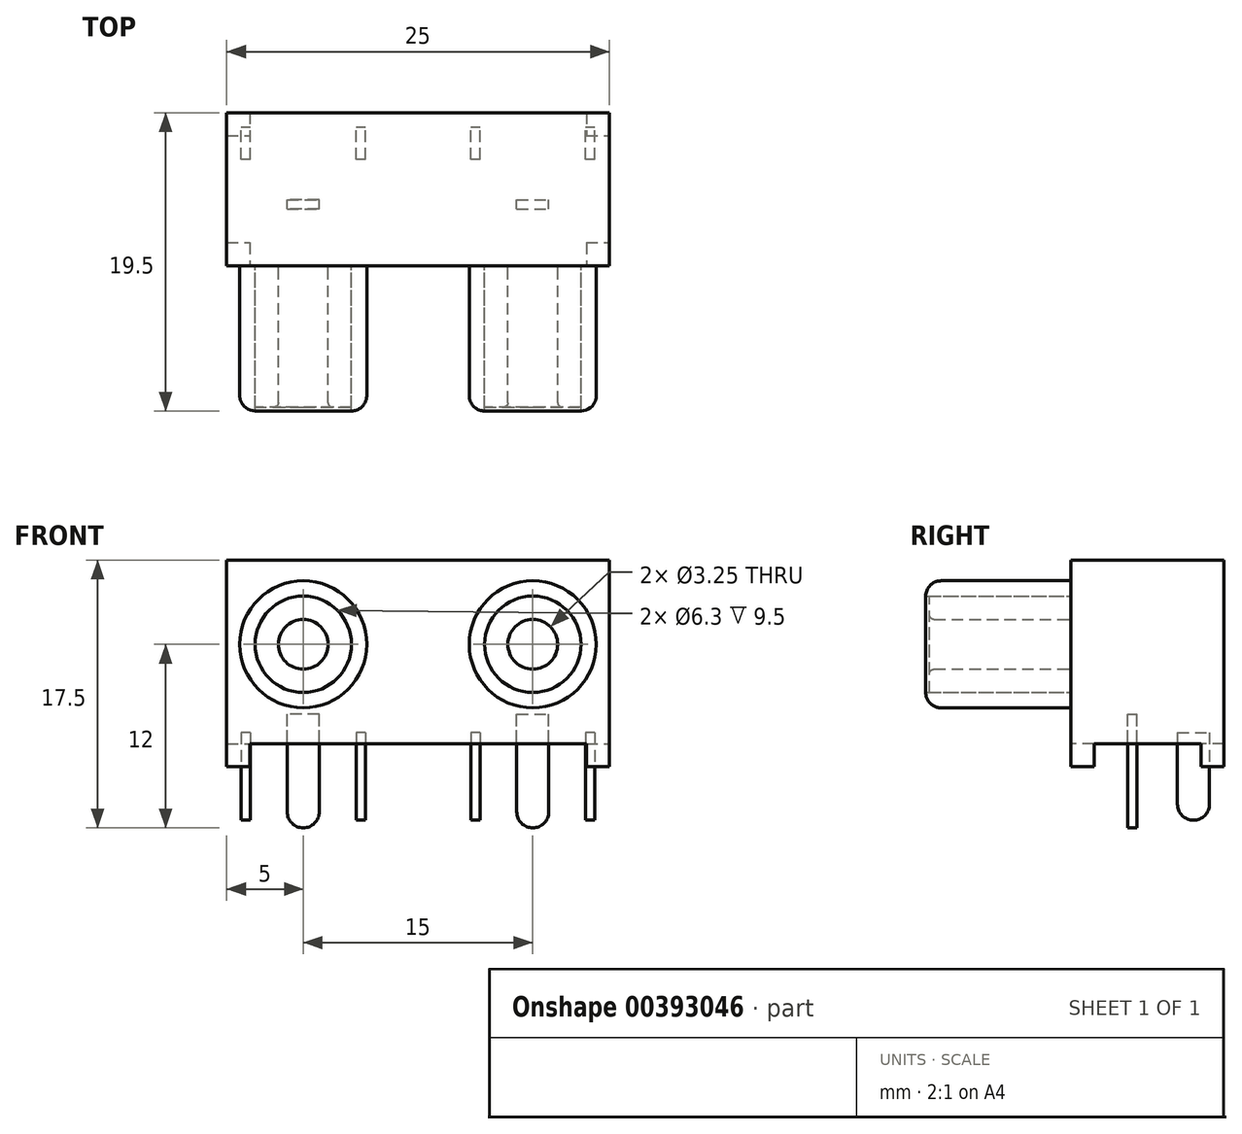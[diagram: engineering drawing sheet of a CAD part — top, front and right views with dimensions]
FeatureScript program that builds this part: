
annotation { "Feature Type Name" : "Feature", "Feature Type Description" : "" }
export const myFeature = defineFeature(function(context is Context, id is Id, definition is map)
    precondition{}
    {
        {
            var Q0;
            Q0=qCreatedBy(makeId("Front.planeOp"),FACE);
            var sketch = newSketch(context, id + "F0", { "sketchPlane" : qUnion([Q0])});
            skCircle(sketch, "E0", {"center": v(-7.5, 0) * mm, "radius": 4.15 * mm});
            skCircle(sketch, "E1", {"center": v(7.5, 0) * mm, "radius": 4.15 * mm});
            skLineSegment(sketch, "E2", {"start": v(-12.5, 5.5) * mm, "end": v(12.5, 5.5) * mm});
            skLineSegment(sketch, "E3", {"start": v(12.5, 5.5) * mm, "end": v(12.5, -8) * mm});
            skLineSegment(sketch, "E4", {"start": v(12.5, -8) * mm, "end": v(11, -8) * mm});
            skLineSegment(sketch, "E5", {"start": v(11, -8) * mm, "end": v(11, -6.5) * mm});
            skLineSegment(sketch, "E6", {"start": v(11, -6.5) * mm, "end": v(-11, -6.5) * mm});
            skLineSegment(sketch, "E7", {"start": v(-11, -6.5) * mm, "end": v(-11, -8) * mm});
            skLineSegment(sketch, "E8", {"start": v(-12.5, 5.5) * mm, "end": v(-12.5, -8) * mm});
            skLineSegment(sketch, "E9", {"start": v(-12.5, -8) * mm, "end": v(-11, -8) * mm});
            skCircle(sketch, "E10", {"center": v(-7.5, 0) * mm, "radius": 1.63 * mm});
            skCircle(sketch, "E11", {"center": v(7.5, 0) * mm, "radius": 1.63 * mm});
            skCircle(sketch, "E12", {"center": v(-7.5, 0) * mm, "radius": 3.15 * mm});
            skCircle(sketch, "E13", {"center": v(7.5, 0) * mm, "radius": 3.15 * mm});
            skSolve(sketch);
        }
        {
            var Q0;
            Q0=makeQuery(id+"F0.imprint","IMPRINT",FACE,{"disambiguationData":[TD([[makeQuery(id+"F0.imprint","IMPRINT",EDGE,{"derivedFrom":sQuery(id+"F0.wireOp",EDGE,"E0")}),1.0]])]});
            var Q1;
            Q1=makeQuery(id+"F0.imprint","IMPRINT",FACE,{"disambiguationData":[TD([[makeQuery(id+"F0.imprint","IMPRINT",EDGE,{"derivedFrom":sQuery(id+"F0.wireOp",EDGE,"E1")}),1.0]])]});
            extrude(context, id + "F1", {"entities" : qUnion([Q0, Q1]), "depth" : 9.5 * mm});
        }
        {
            var Q0;
            Q0=makeQuery(id+"F0.imprint","IMPRINT",FACE,{"disambiguationData":[TD([[makeQuery(id+"F0.imprint","IMPRINT",EDGE,{"derivedFrom":sQuery(id+"F0.wireOp",EDGE,"E10")}),-1.0]])]});
            var Q1;
            Q1=makeQuery(id+"F0.imprint","IMPRINT",FACE,{"disambiguationData":[TD([[makeQuery(id+"F0.imprint","IMPRINT",EDGE,{"derivedFrom":sQuery(id+"F0.wireOp",EDGE,"E11")}),-1.0]])]});
            extrude(context, id + "F2", {"entities" : qUnion([Q0, Q1]), "depth" : 9.25 * mm});
        }
        {
            var Q0;
            Q0=makeQuery(id+"F1.opExtrude","CAP_EDGE",EDGE,{"disambiguationData":[OSD([sQuery(id+"F0.wireOp",EDGE,"E0")])],"isStart":false});
            var Q1;
            Q1=makeQuery(id+"F1.opExtrude","CAP_EDGE",EDGE,{"disambiguationData":[OSD([sQuery(id+"F0.wireOp",EDGE,"E1")])],"isStart":false});
            fillet(context, id + "F3", {"entities" : qUnion([Q0, Q1]), "radius" : 1 * mm, "tangentPropagation" : true, "allowEdgeOverflow" : false});
        }
        {
            var Q0;
            Q0=makeQuery(id+"F0.imprint","IMPRINT",FACE,{"disambiguationData":[TD([[makeQuery(id+"F0.imprint","IMPRINT",EDGE,{"derivedFrom":sQuery(id+"F0.wireOp",EDGE,"E0")}),-1.0]])]});
            var Q1;
            Q1=makeQuery(id+"F0.imprint","IMPRINT",FACE,{"disambiguationData":[TD([[makeQuery(id+"F0.imprint","IMPRINT",EDGE,{"derivedFrom":sQuery(id+"F0.wireOp",EDGE,"E1")}),1.0]])]});
            var Q2;
            Q2=makeQuery(id+"F0.imprint","IMPRINT",FACE,{"disambiguationData":[TD([[makeQuery(id+"F0.imprint","IMPRINT",EDGE,{"derivedFrom":sQuery(id+"F0.wireOp",EDGE,"E11")}),-1.0]])]});
            var Q3;
            Q3=makeQuery(id+"F0.imprint","IMPRINT",FACE,{"disambiguationData":[TD([[makeQuery(id+"F0.imprint","IMPRINT",EDGE,{"derivedFrom":sQuery(id+"F0.wireOp",EDGE,"E11")}),1.0]])]});
            var Q4;
            Q4=makeQuery(id+"F0.imprint","IMPRINT",FACE,{"disambiguationData":[TD([[makeQuery(id+"F0.imprint","IMPRINT",EDGE,{"derivedFrom":sQuery(id+"F0.wireOp",EDGE,"E10")}),-1.0]])]});
            var Q5;
            Q5=makeQuery(id+"F0.imprint","IMPRINT",FACE,{"disambiguationData":[TD([[makeQuery(id+"F0.imprint","IMPRINT",EDGE,{"derivedFrom":sQuery(id+"F0.wireOp",EDGE,"E0")}),1.0]])]});
            var Q6;
            Q6=makeQuery(id+"F0.imprint","IMPRINT",FACE,{"disambiguationData":[TD([[makeQuery(id+"F0.imprint","IMPRINT",EDGE,{"derivedFrom":sQuery(id+"F0.wireOp",EDGE,"E10")}),1.0]])]});
            extrude(context, id + "F4", {"entities" : qUnion([Q0, Q1, Q2, Q3, Q4, Q5, Q6]), "oppositeDirection" : true, "depth" : 10 * mm});
        }
        {
            var Q0;
            Q0=makeQuery(id+"F4.opExtrude","SWEPT_FACE",FACE,{"disambiguationData":[OSD([sQuery(id+"F0.wireOp",EDGE,"E3")])]});
            cPlane(context, id + "F5", {"entities" : qUnion([Q0]), "cplaneType" : CPlaneType.OFFSET, "offset" : 0 * mm, "width" : 150 * mm, "height" : 150 * mm});
        }
        {
            var Q0;
            Q0=qCreatedBy(id+"F5.planeOp",FACE);
            var sketch = newSketch(context, id + "F6", { "sketchPlane" : qUnion([Q0])});
            skLineSegment(sketch, "E14", {"start": v(1.5, -8) * mm, "end": v(1.5, -6.5) * mm});
            skLineSegment(sketch, "E15", {"start": v(1.5, -6.5) * mm, "end": v(8.5, -6.5) * mm});
            skLineSegment(sketch, "E16", {"start": v(8.5, -6.5) * mm, "end": v(8.5, -8) * mm});
            skLineSegment(sketch, "E17", {"start": v(1.5, -8) * mm, "end": v(8.5, -8) * mm});
            skSolve(sketch);
        }
        {
            var Q0;
            Q0=makeQuery(id+"F6.imprint","IMPRINT",FACE,{"disambiguationData":[TD([[makeQuery(id+"F6.imprint","IMPRINT",EDGE,{"derivedFrom":sQuery(id+"F6.wireOp",EDGE,"E14")}),-1.0]])]});
            extrude(context, id + "F7", {"entities" : qUnion([Q0]), "operationType" : NewBodyOperationType.REMOVE, "oppositeDirection" : true, "depth" : 25 * mm});
        }
        {
            var Q0;
            Q0=qCreatedBy(makeId("Front.planeOp"),FACE);
            cPlane(context, id + "F8", {"entities" : qUnion([Q0]), "cplaneType" : CPlaneType.OFFSET, "offset" : 4 * mm, "oppositeDirection" : true, "width" : 150 * mm, "height" : 150 * mm});
        }
        {
            var Q0;
            Q0=qCreatedBy(id+"F8.planeOp",FACE);
            var sketch = newSketch(context, id + "F9", { "sketchPlane" : qUnion([Q0])});
            skLineSegment(sketch, "E18.top", {"start": v(-6.45, -4.58) * mm, "end": v(-8.55, -4.58) * mm});
            skLineSegment(sketch, "E18.left", {"start": v(-6.45, -10.95) * mm, "end": v(-6.45, -4.58) * mm});
            skLineSegment(sketch, "E18.right", {"start": v(-8.55, -10.95) * mm, "end": v(-8.55, -4.58) * mm});
            skArc(sketch, "E19", {"start": v(-8.55, -10.95) * mm, "mid": v(-7.5, -12) * mm, "end": v(-6.45, -10.95) * mm});
            skLineSegment(sketch, "E20.MirrorCS", {"start": v(8.55, -10.95) * mm, "end": v(8.55, -4.58) * mm});
            skLineSegment(sketch, "E21.MirrorCS", {"start": v(6.45, -10.95) * mm, "end": v(6.45, -4.58) * mm});
            skLineSegment(sketch, "E22.MirrorCS", {"start": v(6.45, -4.58) * mm, "end": v(8.55, -4.58) * mm});
            skArc(sketch, "E23.MirrorCS", {"start": v(8.55, -10.95) * mm, "mid": v(7.5, -12) * mm, "end": v(6.45, -10.95) * mm});
            skSolve(sketch);
        }
        {
            var Q0;
            Q0=makeQuery(id+"F9.imprint","IMPRINT",FACE,{"disambiguationData":[TD([[makeQuery(id+"F9.imprint","IMPRINT",EDGE,{"derivedFrom":sQuery(id+"F9.wireOp",EDGE,"E18.top")}),1.0]])]});
            var Q1;
            Q1=makeQuery(id+"F9.imprint","IMPRINT",FACE,{"disambiguationData":[TD([[makeQuery(id+"F9.imprint","IMPRINT",EDGE,{"derivedFrom":sQuery(id+"F9.wireOp",EDGE,"E20.MirrorCS")}),1.0]])]});
            extrude(context, id + "F10", {"entities" : qUnion([Q0, Q1]), "depth" : 0.3 * mm, "hasSecondDirection" : true, "secondDirectionOppositeDirection" : true, "secondDirectionDepth" : 0.3 * mm});
        }
        {
            var Q0;
            Q0=qCreatedBy(makeId("Right.planeOp"),FACE);
            cPlane(context, id + "F11", {"entities" : qUnion([Q0]), "cplaneType" : CPlaneType.OFFSET, "offset" : 3.75 * mm, "width" : 150 * mm, "height" : 150 * mm});
        }
        {
            var Q0;
            Q0=qCreatedBy(makeId("Right.planeOp"),FACE);
            cPlane(context, id + "F12", {"entities" : qUnion([Q0]), "cplaneType" : CPlaneType.OFFSET, "offset" : 11.25 * mm, "width" : 150 * mm, "height" : 150 * mm});
        }
        {
            var Q0;
            Q0=qCreatedBy(makeId("Right.planeOp"),FACE);
            cPlane(context, id + "F13", {"entities" : qUnion([Q0]), "cplaneType" : CPlaneType.OFFSET, "offset" : 3.75 * mm, "oppositeDirection" : true, "width" : 150 * mm, "height" : 150 * mm});
        }
        {
            var Q0;
            Q0=qCreatedBy(makeId("Right.planeOp"),FACE);
            cPlane(context, id + "F14", {"entities" : qUnion([Q0]), "cplaneType" : CPlaneType.OFFSET, "offset" : 11.25 * mm, "oppositeDirection" : true, "width" : 150 * mm, "height" : 150 * mm});
        }
        {
            var Q0;
            Q0=qCreatedBy(id+"F12.planeOp",FACE);
            var sketch = newSketch(context, id + "F15", { "sketchPlane" : qUnion([Q0])});
            skLineSegment(sketch, "E24.bottom", {"start": v(6.95, -5.78) * mm, "end": v(9.05, -5.78) * mm});
            skLineSegment(sketch, "E24.left", {"start": v(6.95, -5.78) * mm, "end": v(6.95, -10.45) * mm});
            skLineSegment(sketch, "E24.right", {"start": v(9.05, -5.78) * mm, "end": v(9.05, -10.45) * mm});
            skArc(sketch, "E25", {"start": v(6.95, -10.45) * mm, "mid": v(8, -11.5) * mm, "end": v(9.05, -10.45) * mm});
            skSolve(sketch);
        }
        {
            var Q0;
            Q0=qCreatedBy(id+"F11.planeOp",FACE);
            var sketch = newSketch(context, id + "F16", { "sketchPlane" : qUnion([Q0])});
            skLineSegment(sketch, "E26.bottom", {"start": v(6.95, -5.78) * mm, "end": v(9.05, -5.78) * mm});
            skLineSegment(sketch, "E26.left", {"start": v(6.95, -5.78) * mm, "end": v(6.95, -10.45) * mm});
            skLineSegment(sketch, "E26.right", {"start": v(9.05, -5.78) * mm, "end": v(9.05, -10.45) * mm});
            skArc(sketch, "E27", {"start": v(6.95, -10.45) * mm, "mid": v(8, -11.5) * mm, "end": v(9.05, -10.45) * mm});
            skSolve(sketch);
        }
        {
            var Q0;
            Q0=qCreatedBy(id+"F13.planeOp",FACE);
            var sketch = newSketch(context, id + "F17", { "sketchPlane" : qUnion([Q0])});
            skLineSegment(sketch, "E28.bottom", {"start": v(6.95, -5.78) * mm, "end": v(9.05, -5.78) * mm});
            skLineSegment(sketch, "E28.left", {"start": v(6.95, -5.78) * mm, "end": v(6.95, -10.45) * mm});
            skLineSegment(sketch, "E28.right", {"start": v(9.05, -5.78) * mm, "end": v(9.05, -10.45) * mm});
            skArc(sketch, "E29", {"start": v(6.95, -10.45) * mm, "mid": v(8, -11.5) * mm, "end": v(9.05, -10.45) * mm});
            skSolve(sketch);
        }
        {
            var Q0;
            Q0=qCreatedBy(id+"F14.planeOp",FACE);
            var sketch = newSketch(context, id + "F18", { "sketchPlane" : qUnion([Q0])});
            skLineSegment(sketch, "E30.bottom", {"start": v(6.95, -5.78) * mm, "end": v(9.05, -5.78) * mm});
            skLineSegment(sketch, "E30.left", {"start": v(6.95, -5.78) * mm, "end": v(6.95, -10.45) * mm});
            skLineSegment(sketch, "E30.right", {"start": v(9.05, -5.78) * mm, "end": v(9.05, -10.45) * mm});
            skArc(sketch, "E31", {"start": v(6.95, -10.45) * mm, "mid": v(8, -11.5) * mm, "end": v(9.05, -10.45) * mm});
            skSolve(sketch);
        }
        {
            var Q0;
            Q0=makeQuery(id+"F18.imprint","IMPRINT",FACE,{"disambiguationData":[TD([[makeQuery(id+"F18.imprint","IMPRINT",EDGE,{"derivedFrom":sQuery(id+"F18.wireOp",EDGE,"E30.bottom")}),-1.0]])]});
            var Q1;
            Q1=makeQuery(id+"F17.imprint","IMPRINT",FACE,{"disambiguationData":[TD([[makeQuery(id+"F17.imprint","IMPRINT",EDGE,{"derivedFrom":sQuery(id+"F17.wireOp",EDGE,"E28.bottom")}),-1.0]])]});
            var Q2;
            Q2=makeQuery(id+"F16.imprint","IMPRINT",FACE,{"disambiguationData":[TD([[makeQuery(id+"F16.imprint","IMPRINT",EDGE,{"derivedFrom":sQuery(id+"F16.wireOp",EDGE,"E26.bottom")}),-1.0]])]});
            var Q3;
            Q3=makeQuery(id+"F15.imprint","IMPRINT",FACE,{"disambiguationData":[TD([[makeQuery(id+"F15.imprint","IMPRINT",EDGE,{"derivedFrom":sQuery(id+"F15.wireOp",EDGE,"E24.bottom")}),-1.0]])]});
            extrude(context, id + "F19", {"entities" : qUnion([Q0, Q1, Q2, Q3]), "depth" : 0.3 * mm, "hasSecondDirection" : true, "secondDirectionOppositeDirection" : true, "secondDirectionDepth" : 0.3 * mm});
        }
        {
            var Q0;
            Q0=makeQuery(id+"F2.opExtrude","CAP_EDGE",EDGE,{"disambiguationData":[OSD([sQuery(id+"F0.wireOp",EDGE,"E10")])],"isStart":false});
            var Q1;
            Q1=makeQuery(id+"F2.opExtrude","CAP_EDGE",EDGE,{"disambiguationData":[OSD([sQuery(id+"F0.wireOp",EDGE,"E11")])],"isStart":false});
            fillet(context, id + "F20", {"entities" : qUnion([Q0, Q1]), "radius" : 0.3 * mm, "tangentPropagation" : true, "allowEdgeOverflow" : false});
        }
    });
